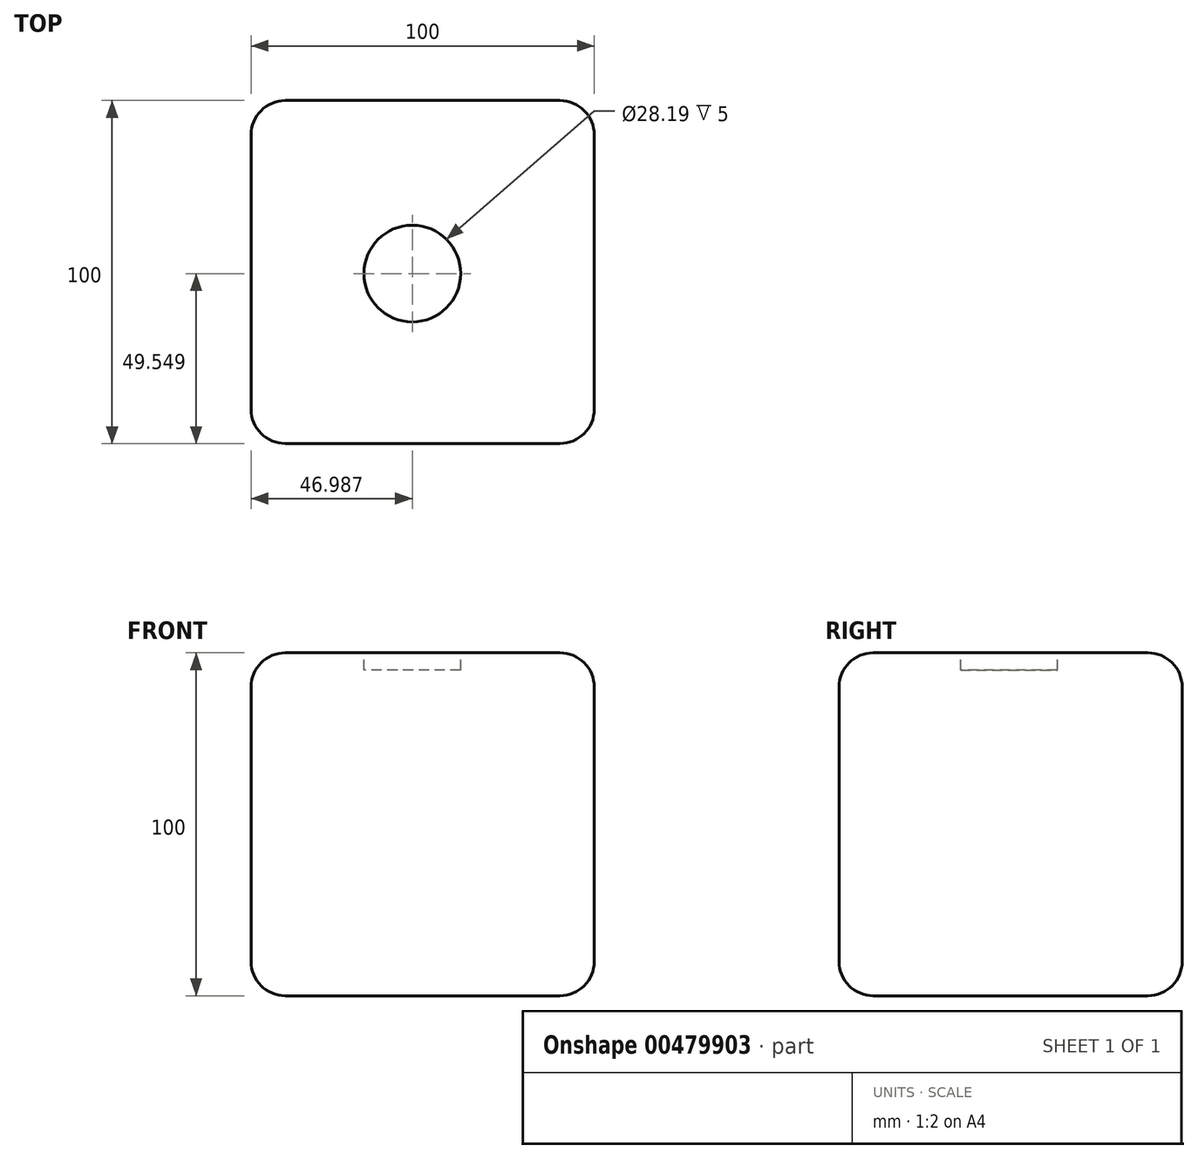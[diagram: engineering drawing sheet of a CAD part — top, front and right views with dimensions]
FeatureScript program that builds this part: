
annotation { "Feature Type Name" : "Feature", "Feature Type Description" : "" }
export const myFeature = defineFeature(function(context is Context, id is Id, definition is map)
    precondition{}
    {
        {
            var Q0;
            Q0=qCreatedBy(makeId("Top.planeOp"),FACE);
            var sketch = newSketch(context, id + "F0", { "sketchPlane" : qUnion([Q0])});
            skLineSegment(sketch, "E0.bottom", {"start": v(-44.83, 38.32) * mm, "end": v(55.17, 38.32) * mm});
            skLineSegment(sketch, "E0.top", {"start": v(-44.83, -61.68) * mm, "end": v(55.17, -61.68) * mm});
            skLineSegment(sketch, "E0.left", {"start": v(-44.83, 38.32) * mm, "end": v(-44.83, -61.68) * mm});
            skLineSegment(sketch, "E0.right", {"start": v(55.17, 38.32) * mm, "end": v(55.17, -61.68) * mm});
            skSolve(sketch);
        }
        {
            var Q0;
            Q0 = qSketchRegion(id + "F0", true);
            extrude(context, id + "F1", {"entities" : qUnion([Q0]), "depth" : 100 * mm, "offsetDistance" : 25 * mm});
        }
        {
            var Q0;
            Q0=makeQuery(id+"F1.opExtrude","CAP_EDGE",EDGE,{"disambiguationData":[OSD([sQuery(id+"F0.wireOp",EDGE,"E0.top")])],"isStart":false});
            var Q1;
            Q1=makeQuery(id+"F1.opExtrude","CAP_EDGE",EDGE,{"disambiguationData":[OSD([sQuery(id+"F0.wireOp",EDGE,"E0.left")])],"isStart":false});
            var Q2;
            Q2=makeQuery(id+"F1.opExtrude","CAP_EDGE",EDGE,{"disambiguationData":[OSD([sQuery(id+"F0.wireOp",EDGE,"E0.right")])],"isStart":false});
            var Q3;
            Q3=makeQuery(id+"F1.opExtrude","CAP_EDGE",EDGE,{"disambiguationData":[OSD([sQuery(id+"F0.wireOp",EDGE,"E0.bottom")])],"isStart":false});
            fillet(context, id + "F2", {"entities" : qUnion([Q0, Q1, Q2, Q3]), "radius" : 10 * mm, "tangentPropagation" : true, "allowEdgeOverflow" : false});
        }
        {
            var Q0;
            Q0=makeQuery(id+"F1.opExtrude","SWEPT_EDGE",EDGE,{"disambiguationData":[OSD([sQuery(id+"F0.wireOp",EDGE,"E0.bottom"),sQuery(id+"F0.wireOp",EDGE,"E0.right")])]});
            var Q1;
            Q1=makeQuery(id+"F1.opExtrude","SWEPT_EDGE",EDGE,{"disambiguationData":[OSD([sQuery(id+"F0.wireOp",EDGE,"E0.top"),sQuery(id+"F0.wireOp",EDGE,"E0.right")])]});
            var Q2;
            Q2=makeQuery(id+"F1.opExtrude","CAP_EDGE",EDGE,{"disambiguationData":[OSD([sQuery(id+"F0.wireOp",EDGE,"E0.right")])],"isStart":true});
            var Q3;
            Q3=makeQuery(id+"F1.opExtrude","SWEPT_EDGE",EDGE,{"disambiguationData":[OSD([sQuery(id+"F0.wireOp",EDGE,"E0.bottom"),sQuery(id+"F0.wireOp",EDGE,"E0.left")])]});
            var Q4;
            Q4=makeQuery(id+"F1.opExtrude","CAP_EDGE",EDGE,{"disambiguationData":[OSD([sQuery(id+"F0.wireOp",EDGE,"E0.left")])],"isStart":true});
            var Q5;
            Q5=makeQuery(id+"F1.opExtrude","CAP_EDGE",EDGE,{"disambiguationData":[OSD([sQuery(id+"F0.wireOp",EDGE,"E0.bottom")])],"isStart":true});
            var Q6;
            Q6=makeQuery(id+"F1.opExtrude","SWEPT_FACE",FACE,{"disambiguationData":[OSD([sQuery(id+"F0.wireOp",EDGE,"E0.left")])]});
            var Q7;
            Q7=makeQuery(id+"F1.opExtrude","CAP_EDGE",EDGE,{"disambiguationData":[OSD([sQuery(id+"F0.wireOp",EDGE,"E0.top")])],"isStart":true});
            var Q8;
            {var subQ0=sQuery(id+"F0.wireOp",EDGE,"E0.top");Q8=makeQuery(id+"F2.opFillet","BLEND_EDGE",EDGE,{"blendedFrom":[makeQuery(id+"F1.opExtrude","CAP_EDGE",EDGE,{"disambiguationData":[OSD([subQ0])],"isStart":false}),makeQuery(id+"F1.opExtrude","SWEPT_FACE",FACE,{"disambiguationData":[OSD([subQ0])]})],"blendedInto":[makeQuery(id+"F1.opExtrude","SWEPT_FACE",FACE,{"disambiguationData":[OSD([subQ0])]})]});}
            fillet(context, id + "F3", {"entities" : qUnion([Q0, Q1, Q2, Q3, Q4, Q5, Q6, Q7, Q8]), "radius" : 10 * mm, "tangentPropagation" : true, "allowEdgeOverflow" : false});
        }
        {
            var Q0;
            Q0=makeQuery(id+"F1.opExtrude","CAP_FACE",FACE,{"disambiguationData":[OSD([sQuery(id+"F0.wireOp",EDGE,"E0.bottom"),sQuery(id+"F0.wireOp",EDGE,"E0.top"),sQuery(id+"F0.wireOp",EDGE,"E0.left"),sQuery(id+"F0.wireOp",EDGE,"E0.right")])],"isStart":false});
            var sketch = newSketch(context, id + "F4", { "sketchPlane" : qUnion([Q0])});
            skCircle(sketch, "E1", {"center": v(2.16, -12.13) * mm, "radius": 14.1 * mm});
            skSolve(sketch);
        }
        {
            var Q0;
            Q0 = qSketchRegion(id + "F4", true);
            extrude(context, id + "F5", {"entities" : qUnion([Q0]), "operationType" : NewBodyOperationType.REMOVE, "oppositeDirection" : true, "depth" : 5 * mm, "offsetDistance" : 25 * mm});
        }
    });
